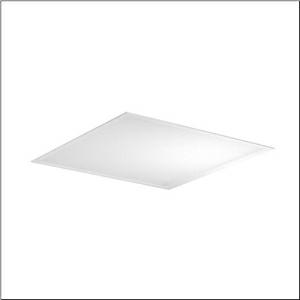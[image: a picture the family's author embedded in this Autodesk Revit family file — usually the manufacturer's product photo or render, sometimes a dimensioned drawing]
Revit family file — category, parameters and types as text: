
# Revit family: apollon_21_square_51mq12w72m14
name_source: partatom
category: Lighting Fixtures
units: mm (PartAtom-declared; Revit-internal decimal feet)

## family parameters
Cut with Voids When Loaded = No
Host = Face
Light Source = No
Part Type = Normal
Room Calculation Point = No
Round Connector Dimension = Use Diameter
Shared = No

## types (1)
- --- (1 x LED, 4200 lm, 24.2 W, 4000K)
    Apparent Load = 24 VA
    CIE Flux Codes = 60 87 97 100 100
    Color Rendering = 80
    Color Temperature = 4000K
    Default Elevation = 1800 mm
    Description = Apollon 21 square, office luminaire, primary optical cover: micro prismatic cover, of PMMA, CAT 2 (L<= 3000cd/m²), light emission: direct distribution, primary light characteristic: symmetric, installation type: lay-in mounting, LED, rated luminous flux: 4.200lm, luminous efficacy: 174lm/W, light colour: 830/840, colour temperature: 3000/4000K, control gear: ON/OFF, with terminal, 3-pole, mains connection: 220..240V, AC/DC, 0/50..60Hz, rated input power: 24.2W, suitable for self-contained emergency lighting element 59MQE002602A with integrated self-test function according to EN 60598-2-22, housing, of aluminium, coated, traffic white (RAL 9016), module: M600, length: 595mm, width: 595mm, height: 55mm, recess depth: 180mm, housing upper side, of sheet steel, galvanised, protection rating (complete): IP20, protection rating (lamp compartment, on room side): IP50, insulation class (complete): insulation class II (safety insulation), certification: CE, ENEC, impact resistance: IK03, permissible operating ambient temperature: -20..+45°C, permissible storage temperature: -40..+80°C, standard: EN 60598-2-22, packaging unit: 1 piece
    Height = 0 mm  [stored 0 ft]
    Lamp = 1 x LED
    Lamp Light Flux = 4200 lm
    Lamp Power = 24.2 W
    Lamp count = 1
    Length = 595 mm
    Luminous efficacy = 174 lm/W
    Manufacturer = Siteco
    ModVariant = No
    Model = 51MQ12W72M14
    Mounting Place = Ceiling
    Mounting Type = Recessed
    Number of Poles = 1
    OnlyDefault = Yes
    Power Factor = 1
    Product Name = Apollon 21 square
    Product group = office luminaire | ceiling recessed
    ProductGroupID = 400
    Protection Class = Protection class II
    Protection Degree = IP 20
    RLX_Detail_Level = 1
    RLX_Emergency_Light_Flux = 0 lm
    RLX_Emergency_Type = 0
    RLX_Emergency_Type_DB = No
    RlxData = <blob elided: 12921 chars, md5=603089dd>
    Socket = socket
    Standby Power = 0 W
    System Light Flux = 4200 lm
    System Power = 24 W
    Type Comments = factory setting
    Type Image = l_1291049.jpg
    URL = http://relux.com
    VarID = @adj_089635
    Voltage = 0 V
    Weight = 0.00 kg
    Width = 595 mm

note: [stored X ft] marks values corroborated as IEEE doubles in the binary element streams (Revit-internal decimal feet)

## geometry (parser evidence)
native form markers: Sweep x10
no freeform markers — native parametric forms only
